# Revit family: TL 2D_Tracklok_SPT-10
name_source: partatom
category: Detail Items
revit_build: Autodesk Revit 2016 (Build: 20150714_1515(x64)
units: mm (PartAtom-declared; Revit-internal decimal feet)

## family parameters
Rotate with component = No
Shared = No

## types (13) — shared parameters

## per-type parameters (varying)
| type | End Elevation | Gaplok End | Gaplok Plan | Gaplok Side | Plan | Side Elevation | Tracklok Retro | Tracklok Retro-Plan | Tracklok Std | Tracklok Timba | Tracklok Timba - Plan |
| Std-Plan | No | No | No | No | Yes | No | No | No | Yes | No | No |
| Std-Side | No | No | No | No | No | Yes | No | No | No | No | No |
| Std-End | Yes | No | No | No | No | No | No | No | No | No | No |
| Bracket to level above | No | No | No | Yes | No | No | No | Yes | No | No | No |
| Retro-End | Yes | No | No | No | No | No | Yes | No | No | No | No |
| Timba-End | Yes | No | No | No | No | No | No | No | No | Yes | No |
| Retro-Plan | No | No | No | No | Yes | No | No | Yes | Yes | No | No |
| Timba-Plan | No | No | No | No | Yes | No | No | No | No | No | Yes |
| Retro-Side | No | No | No | No | No | Yes | Yes | No | No | No | No |
| Timba-Side | No | No | No | No | No | Yes | No | No | No | Yes | No |
| Gaplok-End | Yes | No | No | Yes | No | No | No | No | No | No | No |
| Gaplok-Side | No | Yes | No | No | No | Yes | No | No | No | No | No |
| Gaplok-Plan | No | No | Yes | No | Yes | No | No | No | Yes | No | No |

type visibility flags (boolean, named after types; folded from table):
- Std-Plan: Yes: (none)
- Std-Side: Yes: (none)
- Std-End: Yes: (none)
- Bracket to level above: Yes: Bracket to level above
- Retro-End: Yes: (none)
- Timba-End: Yes: (none)
- Retro-Plan: Yes: (none)
- Timba-Plan: Yes: (none)
- Retro-Side: Yes: (none)
- Timba-Side: Yes: (none)
- Gaplok-End: Yes: (none)
- Gaplok-Side: Yes: (none)
- Gaplok-Plan: Yes: (none)

## geometry (parser evidence)
native form markers: Sweep x2
no freeform markers — native parametric forms only
